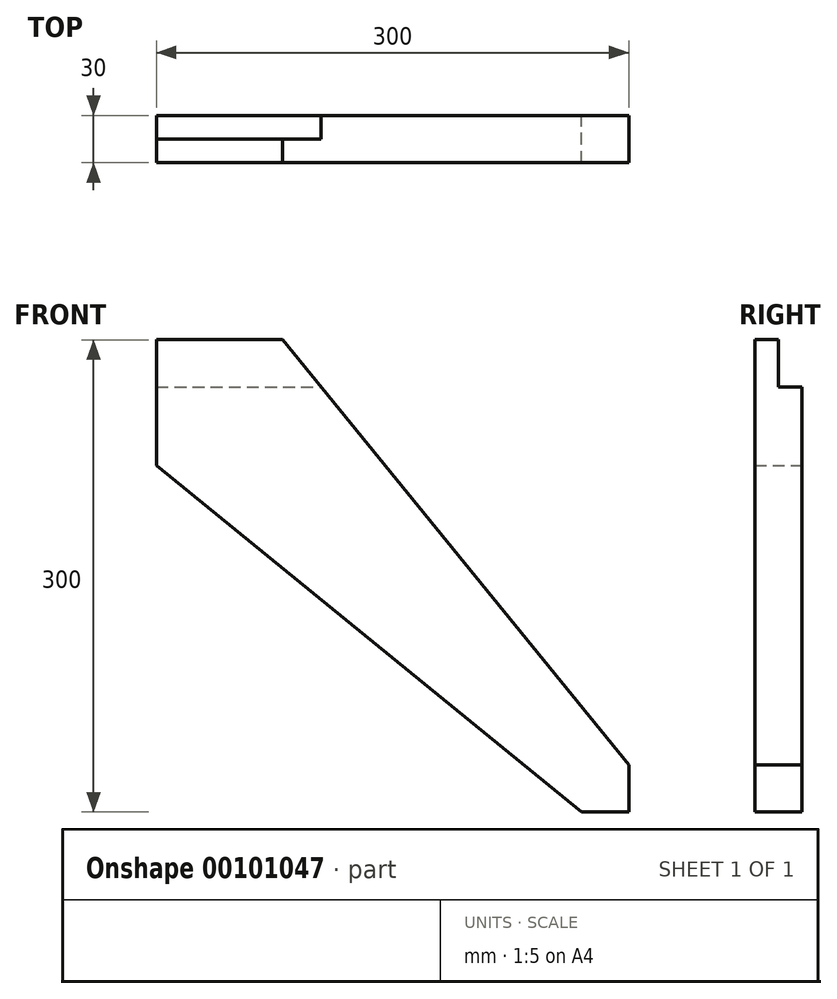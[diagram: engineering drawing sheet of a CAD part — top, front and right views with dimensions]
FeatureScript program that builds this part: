
annotation { "Feature Type Name" : "Feature", "Feature Type Description" : "" }
export const myFeature = defineFeature(function(context is Context, id is Id, definition is map)
    precondition{}
    {
        {
            var Q0;
            Q0=qCreatedBy(makeId("Front.planeOp"),FACE);
            var sketch = newSketch(context, id + "F0", { "sketchPlane" : qUnion([Q0])});
            skLineSegment(sketch, "E0", {"start": v(-184.12, 126.17) * mm, "end": v(-104.12, 126.17) * mm});
            skLineSegment(sketch, "E1", {"start": v(-104.12, 126.17) * mm, "end": v(115.88, -143.83) * mm});
            skLineSegment(sketch, "E2", {"start": v(115.88, -143.83) * mm, "end": v(115.88, -173.83) * mm});
            skLineSegment(sketch, "E3", {"start": v(115.88, -173.83) * mm, "end": v(85.88, -173.83) * mm});
            skLineSegment(sketch, "E4", {"start": v(85.88, -173.83) * mm, "end": v(-184.12, 46.17) * mm});
            skLineSegment(sketch, "E5", {"start": v(-184.12, 46.17) * mm, "end": v(-184.12, 126.17) * mm});
            skLineSegment(sketch, "E6", {"start": v(-184.12, 96.17) * mm, "end": v(-79.67, 96.17) * mm});
            skSolve(sketch);
        }
        {
            var Q0;
            {var subQ1=sQuery(id+"F0.wireOp",EDGE,"E2");Q0=makeQuery(id+"F0.imprint","IMPRINT",FACE,{"disambiguationData":[TD([[makeQuery(id+"F0.imprint","IMPRINT",EDGE,{"derivedFrom":subQ1}),-1.0]])]});}
            var Q1;
            {var subQ0=sQuery(id+"F0.wireOp",EDGE,"E0");Q1=makeQuery(id+"F0.imprint","IMPRINT",FACE,{"disambiguationData":[TD([[makeQuery(id+"F0.imprint","IMPRINT",EDGE,{"derivedFrom":subQ0}),-1.0]])]});}
            extrude(context, id + "F1", {"entities" : qUnion([Q0, Q1]), "depth" : 15 * mm});
        }
        {
            var Q0;
            {var subQ1=sQuery(id+"F0.wireOp",EDGE,"E2");Q0=makeQuery(id+"F0.imprint","IMPRINT",FACE,{"disambiguationData":[TD([[makeQuery(id+"F0.imprint","IMPRINT",EDGE,{"derivedFrom":subQ1}),-1.0]])]});}
            extrude(context, id + "F2", {"entities" : qUnion([Q0]), "operationType" : NewBodyOperationType.ADD, "oppositeDirection" : true, "depth" : 15 * mm});
        }
    });
